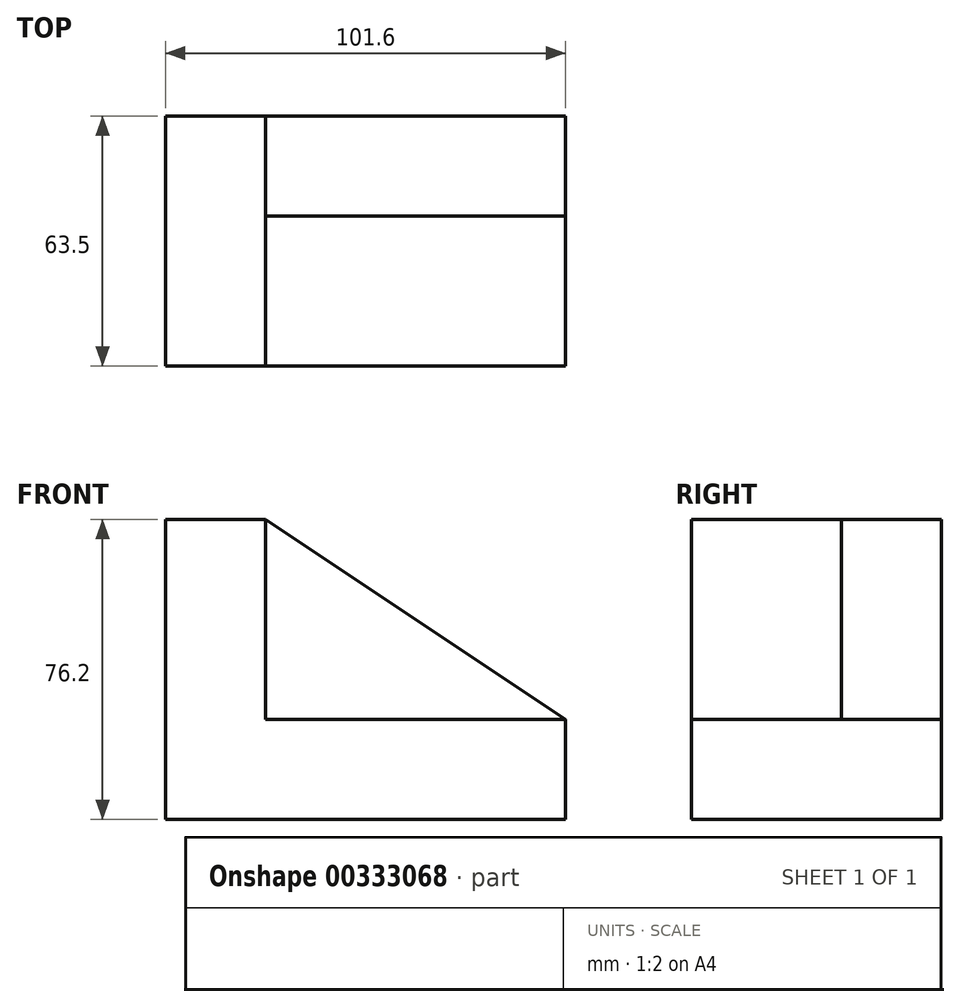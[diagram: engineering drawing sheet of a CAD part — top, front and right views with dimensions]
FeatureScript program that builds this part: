
annotation { "Feature Type Name" : "Feature", "Feature Type Description" : "" }
export const myFeature = defineFeature(function(context is Context, id is Id, definition is map)
    precondition{}
    {
        {
            var Q0;
            Q0=qCreatedBy(makeId("Front.planeOp"),FACE);
            var sketch = newSketch(context, id + "F0", { "sketchPlane" : qUnion([Q0])});
            skLineSegment(sketch, "E0", {"start": v(-19.03, 18.37) * mm, "end": v(-44.43, 18.37) * mm});
            skLineSegment(sketch, "E1", {"start": v(-44.43, 18.37) * mm, "end": v(-44.43, -57.83) * mm});
            skLineSegment(sketch, "E2", {"start": v(-44.43, -57.83) * mm, "end": v(57.17, -57.83) * mm});
            skLineSegment(sketch, "E3", {"start": v(57.17, -57.83) * mm, "end": v(57.17, -32.43) * mm});
            skLineSegment(sketch, "E4", {"start": v(-19.03, 18.37) * mm, "end": v(57.17, -32.43) * mm});
            skSolve(sketch);
        }
        {
            var Q0;
            Q0=makeQuery(id+"F0.imprint","IMPRINT",FACE,{"disambiguationData":[TD([[makeQuery(id+"F0.imprint","IMPRINT",EDGE,{"derivedFrom":sQuery(id+"F0.wireOp",EDGE,"E0")}),1.0]])]});
            extrude(context, id + "F1", {"entities" : qUnion([Q0]), "depth" : 63.5 * mm});
        }
        {
            var Q0;
            Q0=makeQuery(id+"F1.opExtrude","CAP_FACE",FACE,{"disambiguationData":[OSD([sQuery(id+"F0.wireOp",EDGE,"E0"),sQuery(id+"F0.wireOp",EDGE,"E1"),sQuery(id+"F0.wireOp",EDGE,"E2"),sQuery(id+"F0.wireOp",EDGE,"E3"),sQuery(id+"F0.wireOp",EDGE,"E4")])],"isStart":false});
            var sketch = newSketch(context, id + "F2", { "sketchPlane" : qUnion([Q0])});
            skLineSegment(sketch, "E5", {"start": v(-19.03, -32.43) * mm, "end": v(57.17, -32.43) * mm});
            skLineSegment(sketch, "E6", {"start": v(-19.03, 18.37) * mm, "end": v(-19.03, -32.43) * mm});
            skLineSegment(sketch, "E7", {"start": v(-19.03, 18.37) * mm, "end": v(57.17, -32.43) * mm});
            skSolve(sketch);
        }
        {
            var Q0;
            Q0=makeQuery(id+"F2.imprint","IMPRINT",FACE,{"disambiguationData":[TD([[makeQuery(id+"F2.imprint","IMPRINT",EDGE,{"derivedFrom":sQuery(id+"F2.wireOp",EDGE,"E5")}),1.0]])]});
            extrude(context, id + "F3", {"entities" : qUnion([Q0]), "operationType" : NewBodyOperationType.REMOVE, "oppositeDirection" : true, "depth" : 38.1 * mm});
        }
    });
